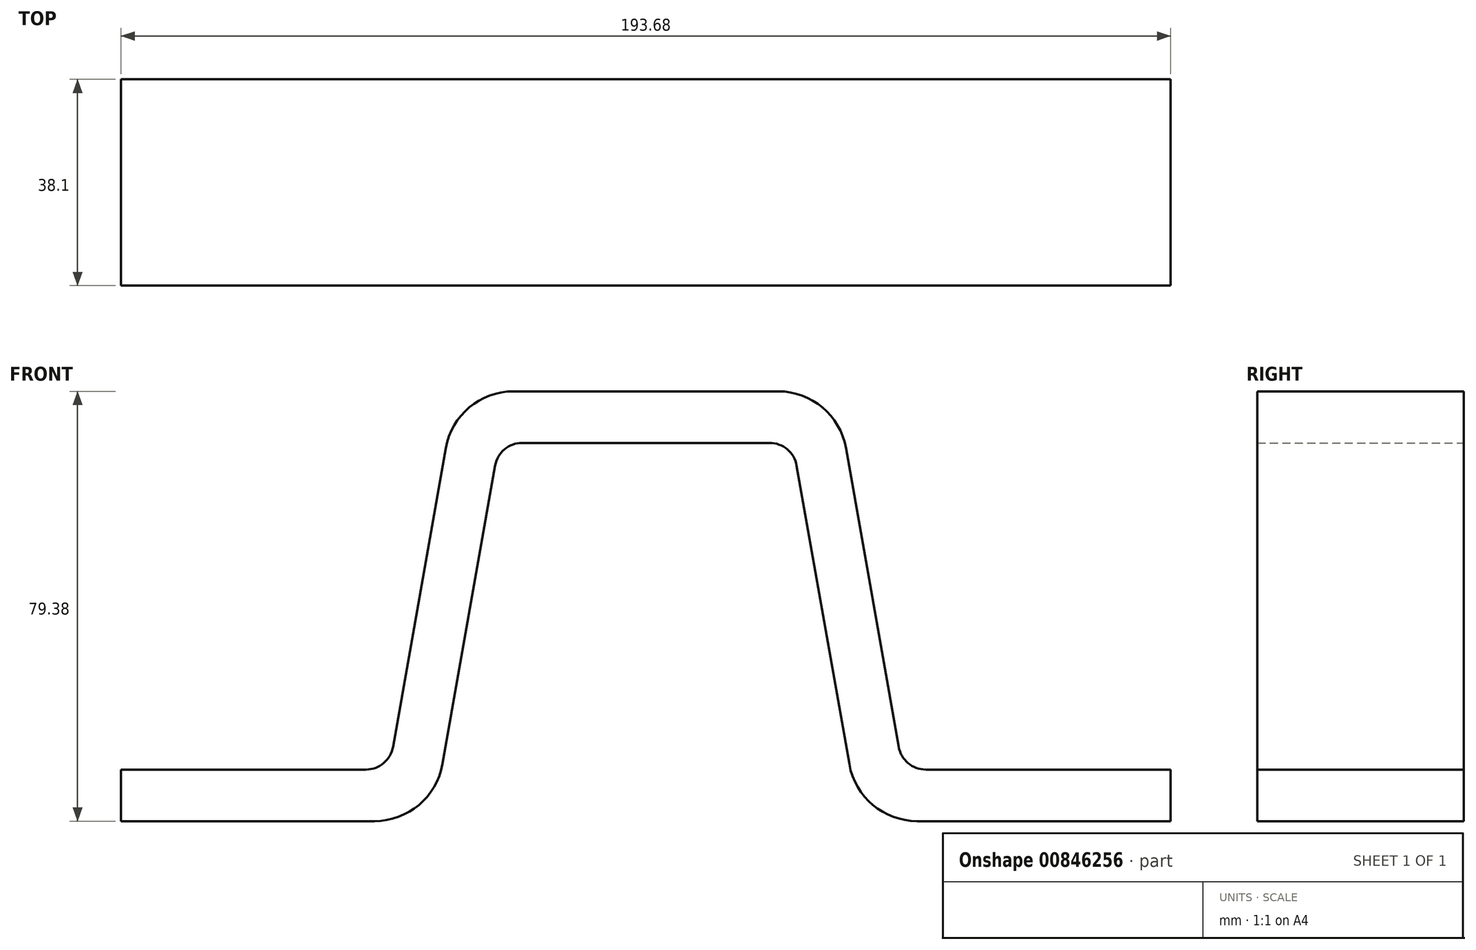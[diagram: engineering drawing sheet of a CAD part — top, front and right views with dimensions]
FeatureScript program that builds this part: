
annotation { "Feature Type Name" : "Feature", "Feature Type Description" : "" }
export const myFeature = defineFeature(function(context is Context, id is Id, definition is map)
    precondition{}
    {
        {
            var Q0;
            Q0=qCreatedBy(makeId("Front.planeOp"),FACE);
            var sketch = newSketch(context, id + "F0", { "sketchPlane" : qUnion([Q0])});
            skLineSegment(sketch, "E0.bottom", {"start": v(96.84, -39.69) * mm, "end": v(39.4, -39.69) * mm});
            skLineSegment(sketch, "E0.top", {"start": v(35.07, 39.69) * mm, "end": v(-35.07, 39.69) * mm});
            skLineSegment(sketch, "E0.left", {"start": v(96.84, -39.69) * mm, "end": v(96.84, -30.16) * mm});
            skLineSegment(sketch, "E0.right", {"start": v(-96.84, -39.69) * mm, "end": v(-96.84, -30.16) * mm});
            skPoint(sketch, "E0.middle", {"position": v(0, 0) * mm});
            skLineSegment(sketch, "E1.0", {"start": v(96.84, -30.16) * mm, "end": v(47.39, -30.16) * mm});
            skLineSegment(sketch, "E2", {"start": v(-27.08, 30.16) * mm, "end": v(-37.72, -30.16) * mm});
            skLineSegment(sketch, "E3.MirrorCS", {"start": v(27.08, 30.16) * mm, "end": v(37.72, -30.16) * mm});
            skLineSegment(sketch, "E4.0", {"start": v(27.08, 30.16) * mm, "end": v(-27.08, 30.16) * mm});
            skLineSegment(sketch, "E5.0", {"start": v(-34.78, 41.34) * mm, "end": v(-47.39, -30.16) * mm});
            skLineSegment(sketch, "E6.0", {"start": v(34.78, 41.34) * mm, "end": v(47.39, -30.16) * mm});
            skLineSegment(sketch, "E7", {"start": v(-37.72, -30.16) * mm, "end": v(-39.4, -39.69) * mm});
            skLineSegment(sketch, "E8", {"start": v(37.72, -30.16) * mm, "end": v(39.4, -39.69) * mm});
            skLineSegment(sketch, "E9.trimOffspring", {"start": v(-47.39, -30.16) * mm, "end": v(-96.84, -30.16) * mm});
            skLineSegment(sketch, "E10.trimOffspring", {"start": v(-39.4, -39.69) * mm, "end": v(-96.84, -39.69) * mm});
            skPoint(sketch, "E11.trimOffspring.end.orphan", {"position": v(96.84, 39.69) * mm});
            skPoint(sketch, "E12.orphan", {"position": v(25.4, 39.69) * mm});
            skPoint(sketch, "E13.orphan", {"position": v(-25.4, 39.69) * mm});
            skPoint(sketch, "E14.orphan", {"position": v(-96.84, 39.69) * mm});
            skSolve(sketch);
        }
        {
            var Q0;
            Q0 = qSketchRegion(id + "F0", true);
            extrude(context, id + "F1", {"entities" : qUnion([Q0]), "depth" : 38.1 * mm, "offsetDistance" : 25.4 * mm});
        }
        {
            var Q0;
            Q0=makeQuery(id+"F1.opExtrude","SWEPT_EDGE",EDGE,{"disambiguationData":[OSD([sQuery(id+"F0.wireOp",EDGE,"E2"),sQuery(id+"F0.wireOp",EDGE,"E4.0")])]});
            var Q1;
            Q1=makeQuery(id+"F1.opExtrude","SWEPT_EDGE",EDGE,{"disambiguationData":[OSD([sQuery(id+"F0.wireOp",EDGE,"E3.MirrorCS"),sQuery(id+"F0.wireOp",EDGE,"E4.0")])]});
            var Q2;
            Q2=makeQuery(id+"F1.opExtrude","SWEPT_EDGE",EDGE,{"disambiguationData":[OSD([sQuery(id+"F0.wireOp",EDGE,"E1.0"),sQuery(id+"F0.wireOp",EDGE,"E6.0")])]});
            var Q3;
            Q3=makeQuery(id+"F1.opExtrude","SWEPT_EDGE",EDGE,{"disambiguationData":[OSD([sQuery(id+"F0.wireOp",EDGE,"E5.0"),sQuery(id+"F0.wireOp",EDGE,"E9.trimOffspring")])]});
            fillet(context, id + "F2", {"entities" : qUnion([Q0, Q1, Q2, Q3]), "radius" : 5.08 * mm, "tangentPropagation" : true, "allowEdgeOverflow" : false});
        }
        {
            var Q0;
            Q0=makeQuery(id+"F1.opExtrude","SWEPT_EDGE",EDGE,{"disambiguationData":[OSD([sQuery(id+"F0.wireOp",EDGE,"E7"),sQuery(id+"F0.wireOp",EDGE,"E10.trimOffspring")])]});
            var Q1;
            Q1=makeQuery(id+"F1.opExtrude","SWEPT_EDGE",EDGE,{"disambiguationData":[OSD([sQuery(id+"F0.wireOp",EDGE,"E0.bottom"),sQuery(id+"F0.wireOp",EDGE,"E8")])]});
            var Q2;
            Q2=makeQuery(id+"F1.opExtrude","SWEPT_EDGE",EDGE,{"disambiguationData":[OSD([sQuery(id+"F0.wireOp",EDGE,"E0.top"),sQuery(id+"F0.wireOp",EDGE,"E6.0")])]});
            var Q3;
            Q3=makeQuery(id+"F1.opExtrude","SWEPT_EDGE",EDGE,{"disambiguationData":[OSD([sQuery(id+"F0.wireOp",EDGE,"E0.top"),sQuery(id+"F0.wireOp",EDGE,"E5.0")])]});
            fillet(context, id + "F3", {"entities" : qUnion([Q0, Q1, Q2, Q3]), "radius" : 12.7 * mm, "tangentPropagation" : true, "allowEdgeOverflow" : false});
        }
    });
